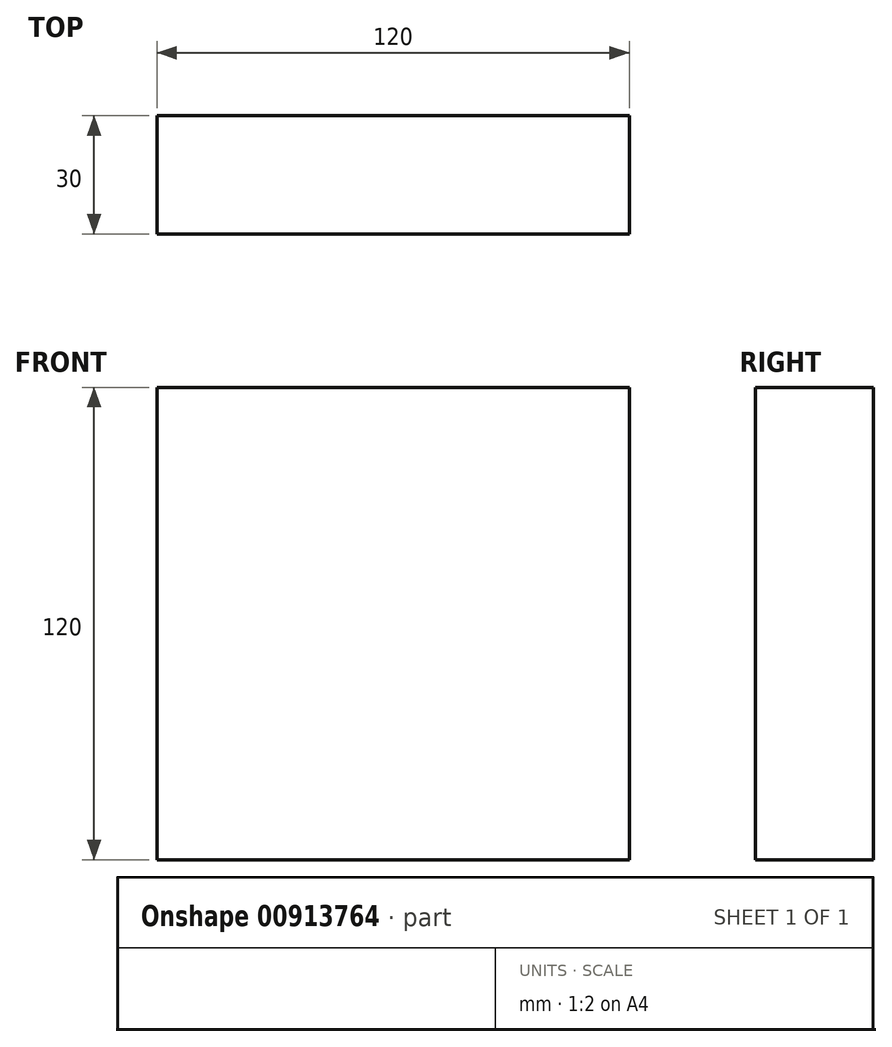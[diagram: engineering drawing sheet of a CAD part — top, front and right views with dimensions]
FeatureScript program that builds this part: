
annotation { "Feature Type Name" : "Feature", "Feature Type Description" : "" }
export const myFeature = defineFeature(function(context is Context, id is Id, definition is map)
    precondition{}
    {
        {
            var Q0;
            Q0=qCreatedBy(makeId("Front.planeOp"),FACE);
            var sketch = newSketch(context, id + "F0", { "sketchPlane" : qUnion([Q0])});
            skLineSegment(sketch, "E0.bottom", {"start": v(0, 0) * mm, "end": v(120, 0) * mm});
            skLineSegment(sketch, "E0.top", {"start": v(0, 120) * mm, "end": v(120, 120) * mm});
            skLineSegment(sketch, "E0.left", {"start": v(0, 0) * mm, "end": v(0, 120) * mm});
            skLineSegment(sketch, "E0.right", {"start": v(120, 0) * mm, "end": v(120, 120) * mm});
            skSolve(sketch);
        }
        {
            var Q0;
            Q0=makeQuery(id+"F0.imprint","IMPRINT",FACE,{"disambiguationData":[TD([[makeQuery(id+"F0.imprint","IMPRINT",EDGE,{"derivedFrom":sQuery(id+"F0.wireOp",EDGE,"E0.bottom")}),1.0]])]});
            extrude(context, id + "F1", {"entities" : qUnion([Q0]), "depth" : 30 * mm, "offsetDistance" : 25.4 * mm});
        }
    });
